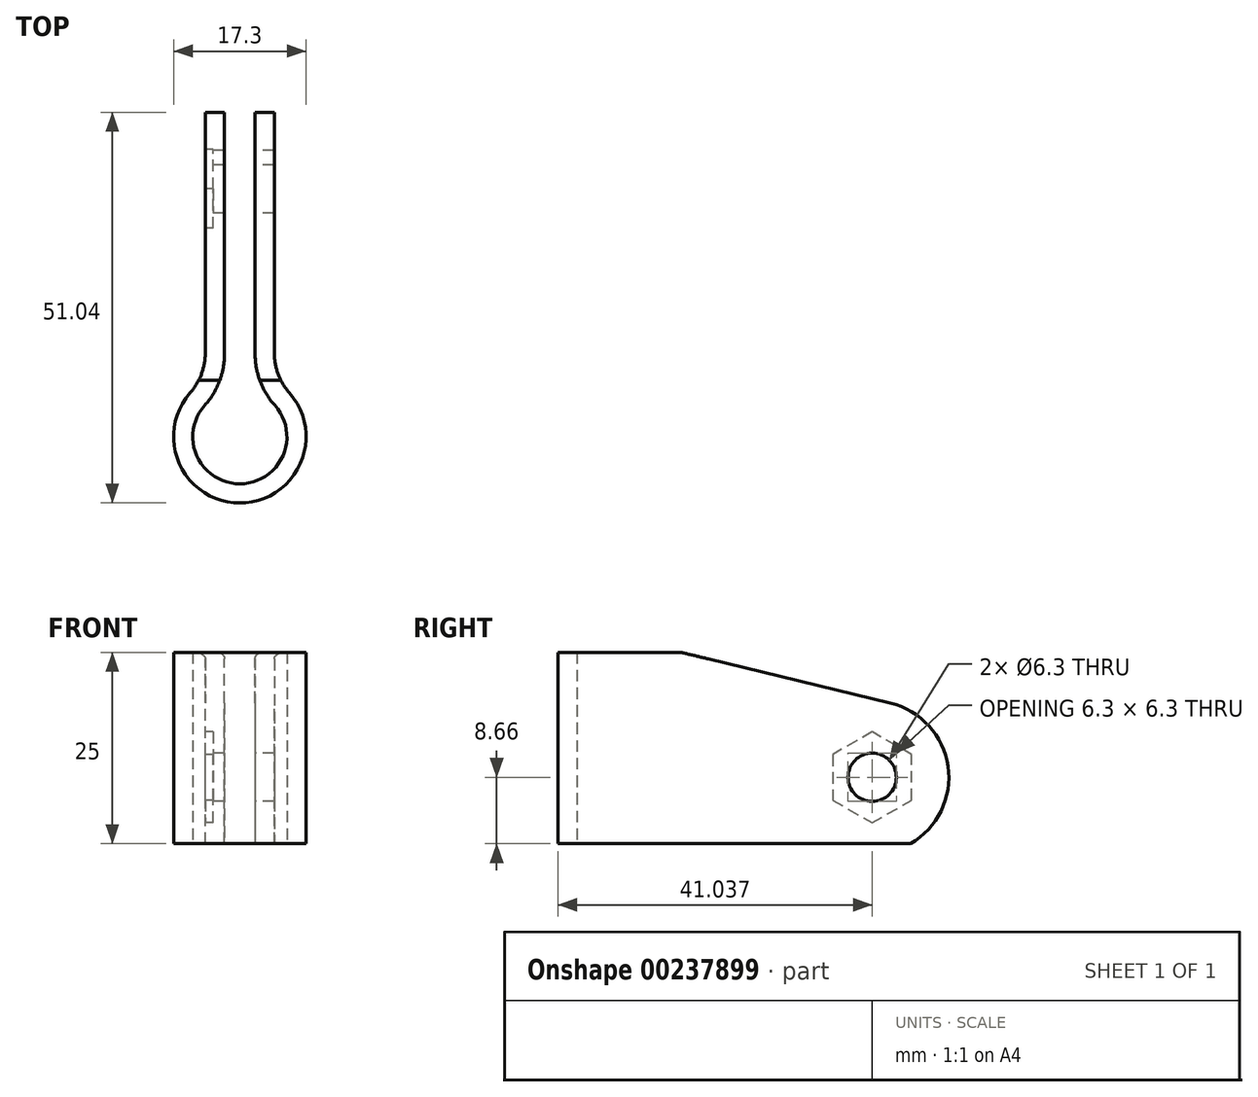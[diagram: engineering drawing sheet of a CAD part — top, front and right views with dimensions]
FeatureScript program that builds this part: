
annotation { "Feature Type Name" : "Feature", "Feature Type Description" : "" }
export const myFeature = defineFeature(function(context is Context, id is Id, definition is map)
    precondition{}
    {
        {
            var Q0;
            Q0=qCreatedBy(makeId("Top.planeOp"),FACE);
            var sketch = newSketch(context, id + "F0", { "sketchPlane" : qUnion([Q0])});
            skCircle(sketch, "E0", {"center": v(0, 0) * mm, "radius": 6.15 * mm});
            skArc(sketch, "E1", {"start": v(-4.5, 7.39) * mm, "mid": v(0, -8.65) * mm, "end": v(4.5, 7.39) * mm});
            skLineSegment(sketch, "E2", {"start": v(4.5, 7.39) * mm, "end": v(-4.5, 7.39) * mm});
            skSolve(sketch);
        }
        {
            var Q0;
            Q0=makeQuery(id+"F0.imprint","IMPRINT",FACE,{"disambiguationData":[TD([[makeQuery(id+"F0.imprint","IMPRINT",EDGE,{"derivedFrom":sQuery(id+"F0.wireOp",EDGE,"E0")}),-1.0]])]});
            extrude(context, id + "F1", {"entities" : qUnion([Q0]), "offsetDistance" : 25 * mm, "depth" : 25 * mm});
        }
        {
            var Q0;
            Q0=qCreatedBy(makeId("Right.planeOp"),FACE);
            var sketch = newSketch(context, id + "F2", { "sketchPlane" : qUnion([Q0])});
            skLineSegment(sketch, "E3", {"start": v(7.39, 25) * mm, "end": v(7.39, 0) * mm});
            skLineSegment(sketch, "E4", {"start": v(7.39, 25) * mm, "end": v(34.74, 18.38) * mm});
            skLineSegment(sketch, "E5", {"start": v(37.39, 0) * mm, "end": v(7.39, 0) * mm});
            skArc(sketch, "E6", {"start": v(37.39, 0) * mm, "mid": v(42.29, 10.09) * mm, "end": v(34.74, 18.38) * mm});
            skLineSegment(sketch, "E7", {"start": v(37.39, 0) * mm, "end": v(49.2, 6.82) * mm, "construction": true});
            skCircle(sketch, "E8", {"center": v(32.39, 8.66) * mm, "radius": 3.15 * mm});
            skSolve(sketch);
        }
        {
            var Q0;
            Q0=makeQuery(id+"F2.imprint","IMPRINT",FACE,{"disambiguationData":[TD([[makeQuery(id+"F2.imprint","IMPRINT",EDGE,{"derivedFrom":sQuery(id+"F2.wireOp",EDGE,"E3")}),1.0]])]});
            extrude(context, id + "F3", {"entities" : qUnion([Q0]), "operationType" : NewBodyOperationType.ADD, "offsetDistance" : 25 * mm, "depth" : 9 * mm, "symmetric" : true});
        }
        {
            var Q0;
            Q0=qCreatedBy(makeId("Top.planeOp"),FACE);
            var sketch = newSketch(context, id + "F4", { "sketchPlane" : qUnion([Q0])});
            skLineSegment(sketch, "E9.bottom", {"start": v(-2, 0) * mm, "end": v(2, 0) * mm});
            skLineSegment(sketch, "E9.top", {"start": v(-2, 43.29) * mm, "end": v(2, 43.29) * mm});
            skLineSegment(sketch, "E9.left", {"start": v(-2, 0) * mm, "end": v(-2, 43.29) * mm});
            skLineSegment(sketch, "E9.right", {"start": v(2, 0) * mm, "end": v(2, 43.29) * mm});
            skSolve(sketch);
        }
        {
            var Q0;
            Q0=makeQuery(id+"F4.imprint","IMPRINT",FACE,{"disambiguationData":[TD([[makeQuery(id+"F4.imprint","IMPRINT",EDGE,{"derivedFrom":sQuery(id+"F4.wireOp",EDGE,"E9.bottom")}),1.0]])]});
            extrude(context, id + "F5", {"entities" : qUnion([Q0]), "operationType" : NewBodyOperationType.REMOVE, "endBound" : BoundingType.THROUGH_ALL, "depth" : 25 * mm});
        }
        {
            var Q0;
            {var subQ0=sQuery(id+"F0.wireOp",EDGE,"E2");var subQ1=sQuery(id+"F0.wireOp",EDGE,"E1");Q0=makeQuery(id+"F3.boolean.opBoolean","MERGE",EDGE,{"derivedFrom":[makeQuery(id+"F1.opExtrude","SWEPT_EDGE",EDGE,{"disambiguationData":[OSD([subQ1,subQ0]),TDD([makeQuery(id+"F0.imprint","INTERSECT",VERTEX,{"disambiguationData":[OD(1.0)],"derivedFrom":[subQ1,subQ0]})])]}),makeQuery(id+"F3.opExtrude","CAP_EDGE",EDGE,{"disambiguationData":[OSD([sQuery(id+"F2.wireOp",EDGE,"E3")])],"isStart":false})]});}
            var Q1;
            {var subQ0=sQuery(id+"F0.wireOp",EDGE,"E2");var subQ1=sQuery(id+"F0.wireOp",EDGE,"E1");Q1=makeQuery(id+"F3.boolean.opBoolean","MERGE",EDGE,{"derivedFrom":[makeQuery(id+"F1.opExtrude","SWEPT_EDGE",EDGE,{"disambiguationData":[OSD([subQ1,subQ0]),TDD([makeQuery(id+"F0.imprint","INTERSECT",VERTEX,{"disambiguationData":[OD(0.0)],"derivedFrom":[subQ1,subQ0]})])]}),makeQuery(id+"F3.opExtrude","CAP_EDGE",EDGE,{"disambiguationData":[OSD([sQuery(id+"F2.wireOp",EDGE,"E3")])],"isStart":true})]});}
            fillet(context, id + "F6", {"entities" : qUnion([Q0, Q1]), "radius" : 8 * mm, "tangentPropagation" : true, "allowEdgeOverflow" : false});
        }
        {
            var Q0;
            Q0=makeQuery(id+"F5.boolean.opBoolean","INTERSECT",EDGE,{"derivedFrom":[makeQuery(id+"F1.opExtrude","SWEPT_FACE",FACE,{"disambiguationData":[OSD([sQuery(id+"F0.wireOp",EDGE,"E0")])]}),makeQuery(id+"F5.opExtrude","SWEPT_FACE",FACE,{"disambiguationData":[OSD([sQuery(id+"F4.wireOp",EDGE,"E9.left")])]})]});
            var Q1;
            Q1=makeQuery(id+"F5.boolean.opBoolean","INTERSECT",EDGE,{"derivedFrom":[makeQuery(id+"F1.opExtrude","SWEPT_FACE",FACE,{"disambiguationData":[OSD([sQuery(id+"F0.wireOp",EDGE,"E0")])]}),makeQuery(id+"F5.opExtrude","SWEPT_FACE",FACE,{"disambiguationData":[OSD([sQuery(id+"F4.wireOp",EDGE,"E9.right")])]})]});
            fillet(context, id + "F7", {"entities" : qUnion([Q0, Q1]), "radius" : 10 * mm, "tangentPropagation" : true, "allowEdgeOverflow" : false});
        }
        {
            var Q0;
            Q0=makeQuery(id+"F3.opExtrude","CAP_FACE",FACE,{"disambiguationData":[OSD([sQuery(id+"F2.wireOp",EDGE,"E3"),sQuery(id+"F2.wireOp",EDGE,"E4"),sQuery(id+"F2.wireOp",EDGE,"E5"),sQuery(id+"F2.wireOp",EDGE,"E6"),sQuery(id+"F2.wireOp",EDGE,"E8")])],"isStart":true});
            var sketch = newSketch(context, id + "F8", { "sketchPlane" : qUnion([Q0])});
            skCircle(sketch, "E10.cCircle", {"center": v(-32.39, 8.66) * mm, "radius": 5.15 * mm, "construction": true});
            skLineSegment(sketch, "E10.0", {"start": v(-37.54, 5.69) * mm, "end": v(-37.54, 11.63) * mm});
            skLineSegment(sketch, "E10.1", {"start": v(-37.54, 11.63) * mm, "end": v(-32.39, 14.6) * mm});
            skLineSegment(sketch, "E10.2", {"start": v(-32.39, 14.6) * mm, "end": v(-27.24, 11.63) * mm});
            skLineSegment(sketch, "E10.3", {"start": v(-27.24, 11.63) * mm, "end": v(-27.24, 5.69) * mm});
            skLineSegment(sketch, "E10.4", {"start": v(-27.24, 5.69) * mm, "end": v(-32.39, 2.71) * mm});
            skLineSegment(sketch, "E10.5", {"start": v(-32.39, 2.71) * mm, "end": v(-37.54, 5.69) * mm});
            skPoint(sketch, "E10.0.midPoint", {"position": v(-37.54, 8.66) * mm});
            skSolve(sketch);
        }
        {
            var Q0;
            Q0=makeQuery(id+"F8.imprint","IMPRINT",FACE,{"disambiguationData":[TD([[makeQuery(id+"F8.imprint","IMPRINT",EDGE,{"derivedFrom":sQuery(id+"F8.wireOp",EDGE,"E10.0")}),-1.0]])]});
            extrude(context, id + "F9", {"entities" : qUnion([Q0]), "operationType" : NewBodyOperationType.REMOVE, "oppositeDirection" : true, "depth" : 1 * mm});
        }
    });
